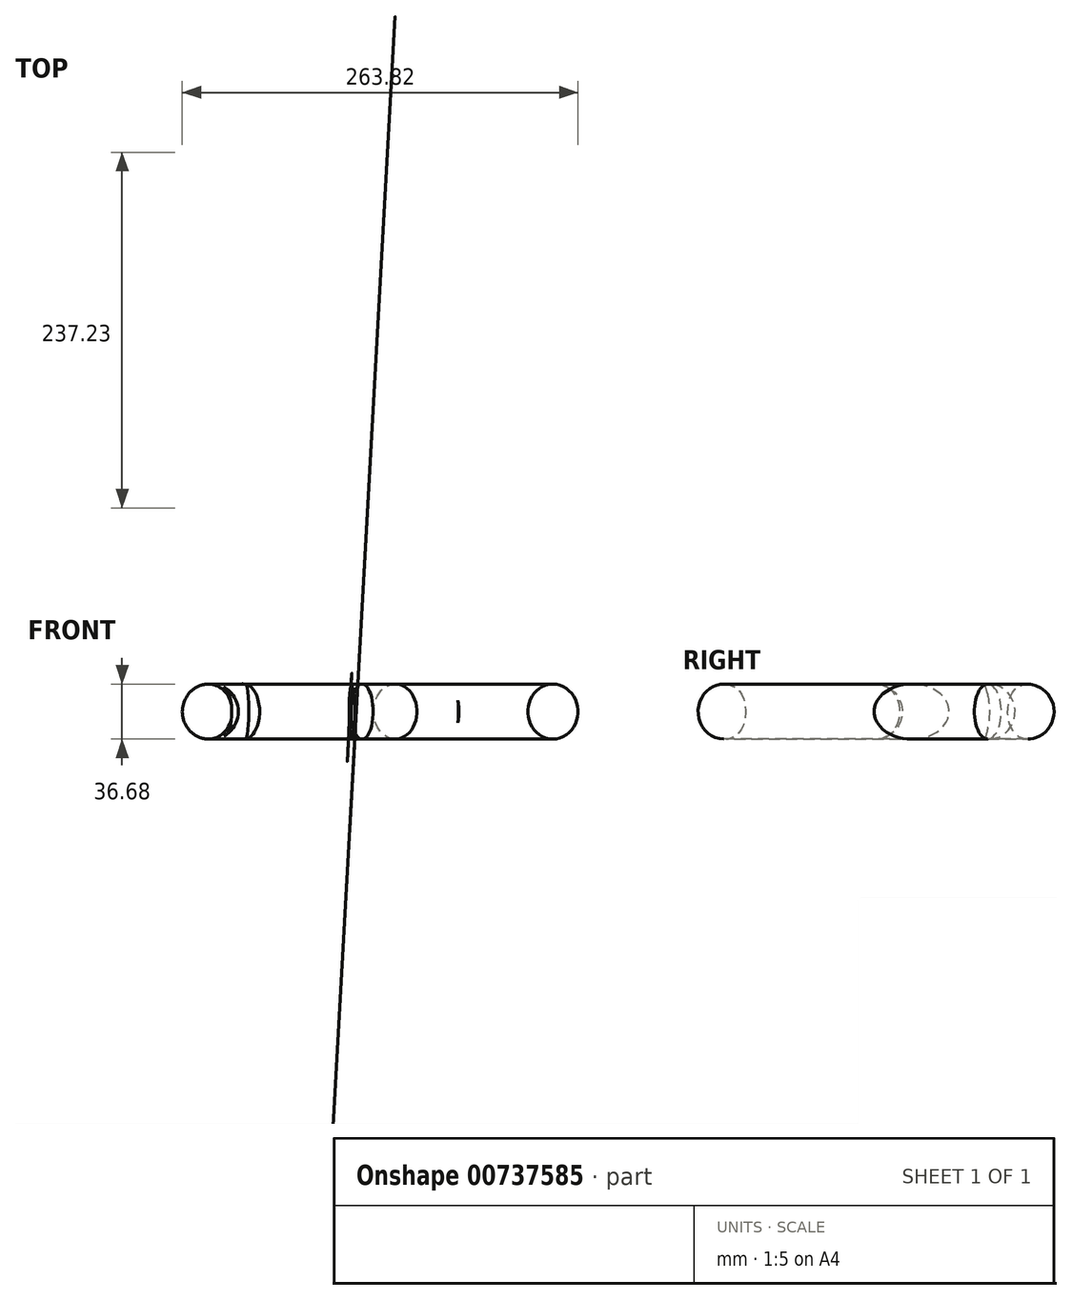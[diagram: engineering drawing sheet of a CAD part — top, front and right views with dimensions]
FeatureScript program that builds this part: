
annotation { "Feature Type Name" : "Feature", "Feature Type Description" : "" }
export const myFeature = defineFeature(function(context is Context, id is Id, definition is map)
    precondition{}
    {
        {
            var Q0;
            Q0=qCreatedBy(makeId("Front.planeOp"),FACE);
            var sketch = newSketch(context, id + "F0", { "sketchPlane" : qUnion([Q0])});
            skCircle(sketch, "E0", {"center": v(2.38, 0) * mm, "radius": 18.34 * mm});
            skSolve(sketch);
        }
        {
            var Q0;
            Q0=qCreatedBy(makeId("Top.planeOp"),FACE);
            var sketch = newSketch(context, id + "F1", { "sketchPlane" : qUnion([Q0])});
            skLineSegment(sketch, "E1", {"start": v(0, 0) * mm, "end": v(21.28, 48.73) * mm});
            skFitSpline(sketch, "E2", {"points": [v(21.28, 48.73) * mm, v(58, 76.49) * mm, v(107.03, 24.83) * mm, v(129.16, -81.36) * mm, v(90.28, -130.53) * mm, v(-3.31, -91.78) * mm, v(-8.03, -89.62) * mm, v(-74.91, -31.32) * mm, v(-78.92, -27.98) * mm, v(-102.84, 45.3) * mm, v(0, 0) * mm], "startDerivative": vector(399.79, 483.07) * mm, "endDerivative": vector(1052.06, -693.05) * mm});
            skSolve(sketch);
        }
        {
            var Q0;
            Q0=makeQuery(id+"F0.imprint","IMPRINT",FACE,{"disambiguationData":[TD([[makeQuery(id+"F0.imprint","IMPRINT",EDGE,{"derivedFrom":sQuery(id+"F0.wireOp",EDGE,"E0")}),1.0]])]});
            var Q1;
            Q1=sQuery(id+"F1.wireOp",EDGE,"E2");
            var Q2;
            Q2=sQuery(id+"F1.wireOp",EDGE,"E1");
            sweep(context, id + "F2", {"profiles" : qUnion([Q0]), "path" : qUnion([Q1, Q2])});
        }
    });
